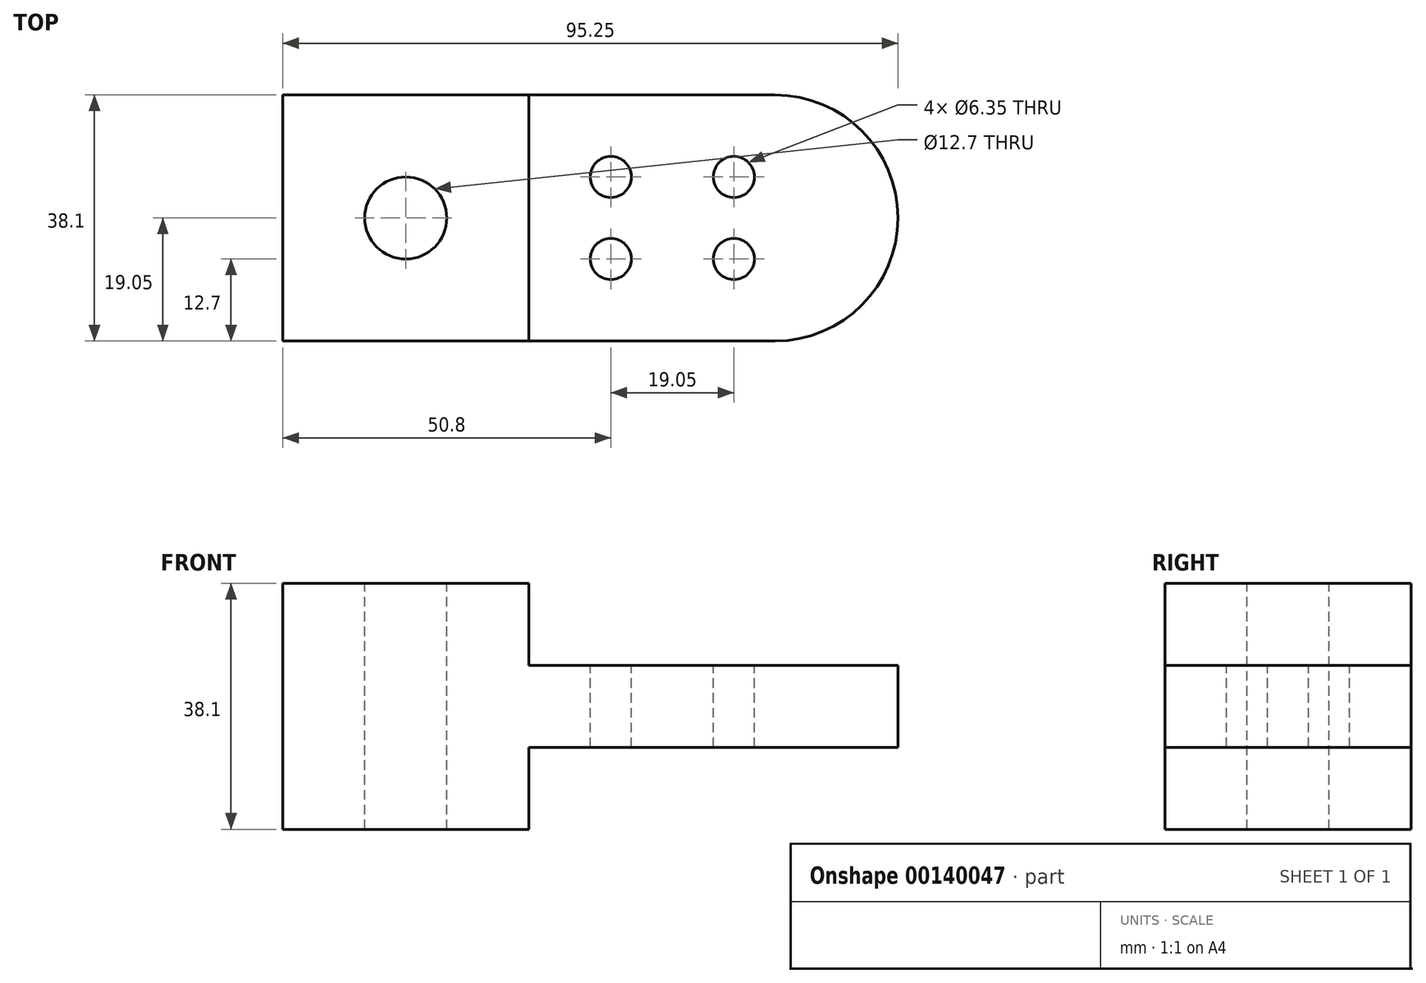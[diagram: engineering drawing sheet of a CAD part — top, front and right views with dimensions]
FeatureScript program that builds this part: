
annotation { "Feature Type Name" : "Feature", "Feature Type Description" : "" }
export const myFeature = defineFeature(function(context is Context, id is Id, definition is map)
    precondition{}
    {
        {
            var Q0;
            Q0=qCreatedBy(makeId("Top.planeOp"),FACE);
            var sketch = newSketch(context, id + "F0", { "sketchPlane" : qUnion([Q0])});
            skLineSegment(sketch, "E0.bottom", {"start": v(0, 0) * mm, "end": v(38.1, 0) * mm});
            skLineSegment(sketch, "E0.top", {"start": v(0, 38.1) * mm, "end": v(38.1, 38.1) * mm});
            skLineSegment(sketch, "E0.left", {"start": v(0, 0) * mm, "end": v(0, 38.1) * mm});
            skLineSegment(sketch, "E0.right", {"start": v(38.1, 0) * mm, "end": v(38.1, 38.1) * mm});
            skLineSegment(sketch, "E1.bottom", {"start": v(38.1, 38.1) * mm, "end": v(76.2, 38.1) * mm});
            skLineSegment(sketch, "E1.top", {"start": v(38.1, 0) * mm, "end": v(76.2, 0) * mm});
            skLineSegment(sketch, "E1.left", {"start": v(38.1, 38.1) * mm, "end": v(38.1, 0) * mm});
            skArc(sketch, "E2", {"start": v(76.2, 0) * mm, "mid": v(95.25, 19.05) * mm, "end": v(76.2, 38.1) * mm});
            skSolve(sketch);
        }
        {
            var Q0;
            Q0=makeQuery(id+"F0.imprint","IMPRINT",FACE,{"disambiguationData":[TD([[makeQuery(id+"F0.imprint","IMPRINT",EDGE,{"derivedFrom":sQuery(id+"F0.wireOp",EDGE,"E0.bottom")}),1.0]])]});
            extrude(context, id + "F1", {"entities" : qUnion([Q0]), "endBound" : BoundingType.SYMMETRIC, "depth" : 38.1 * mm});
        }
        {
            var Q0;
            Q0=makeQuery(id+"F0.imprint","IMPRINT",FACE,{"disambiguationData":[TD([[makeQuery(id+"F0.imprint","IMPRINT",EDGE,{"derivedFrom":sQuery(id+"F0.wireOp",EDGE,"E1.bottom")}),-1.0]])]});
            extrude(context, id + "F2", {"entities" : qUnion([Q0]), "operationType" : NewBodyOperationType.ADD, "endBound" : BoundingType.SYMMETRIC, "depth" : 12.7 * mm});
        }
        {
            var Q0;
            Q0=makeQuery(id+"F1.opExtrude","CAP_FACE",FACE,{"disambiguationData":[OSD([sQuery(id+"F0.wireOp",EDGE,"E0.bottom"),sQuery(id+"F0.wireOp",EDGE,"E0.top"),sQuery(id+"F0.wireOp",EDGE,"E0.left"),sQuery(id+"F0.wireOp",EDGE,"E1.left")])],"isStart":false});
            var sketch = newSketch(context, id + "F3", { "sketchPlane" : qUnion([Q0])});
            skCircle(sketch, "E3", {"center": v(19.05, 19.05) * mm, "radius": 6.35 * mm});
            skPoint(sketch, "E3.centerSnap0", {"position": v(19.05, 38.1) * mm});
            skPoint(sketch, "E3.centerSnap1", {"position": v(0, 19.05) * mm});
            skCircle(sketch, "E4", {"center": v(50.8, 25.4) * mm, "radius": 3.18 * mm});
            skCircle(sketch, "E5", {"center": v(69.85, 25.4) * mm, "radius": 3.18 * mm});
            skCircle(sketch, "E6", {"center": v(50.8, 12.7) * mm, "radius": 3.18 * mm});
            skCircle(sketch, "E7", {"center": v(69.85, 12.7) * mm, "radius": 3.18 * mm});
            skSolve(sketch);
        }
        {
            var Q0;
            Q0=makeQuery(id+"F3.imprint","IMPRINT",FACE,{"disambiguationData":[TD([[makeQuery(id+"F3.imprint","IMPRINT",EDGE,{"derivedFrom":sQuery(id+"F3.wireOp",EDGE,"E3")}),1.0]])]});
            var Q1;
            Q1=makeQuery(id+"F3.imprint","IMPRINT",FACE,{"disambiguationData":[TD([[makeQuery(id+"F3.imprint","IMPRINT",EDGE,{"derivedFrom":sQuery(id+"F3.wireOp",EDGE,"E4")}),1.0]])]});
            var Q2;
            Q2=makeQuery(id+"F3.imprint","IMPRINT",FACE,{"disambiguationData":[TD([[makeQuery(id+"F3.imprint","IMPRINT",EDGE,{"derivedFrom":sQuery(id+"F3.wireOp",EDGE,"E6")}),1.0]])]});
            var Q3;
            Q3=makeQuery(id+"F3.imprint","IMPRINT",FACE,{"disambiguationData":[TD([[makeQuery(id+"F3.imprint","IMPRINT",EDGE,{"derivedFrom":sQuery(id+"F3.wireOp",EDGE,"E7")}),1.0]])]});
            var Q4;
            Q4=makeQuery(id+"F3.imprint","IMPRINT",FACE,{"disambiguationData":[TD([[makeQuery(id+"F3.imprint","IMPRINT",EDGE,{"derivedFrom":sQuery(id+"F3.wireOp",EDGE,"E5")}),1.0]])]});
            extrude(context, id + "F4", {"entities" : qUnion([Q0, Q1, Q2, Q3, Q4]), "operationType" : NewBodyOperationType.REMOVE, "endBound" : BoundingType.THROUGH_ALL, "oppositeDirection" : true, "depth" : 25.4 * mm});
        }
    });
